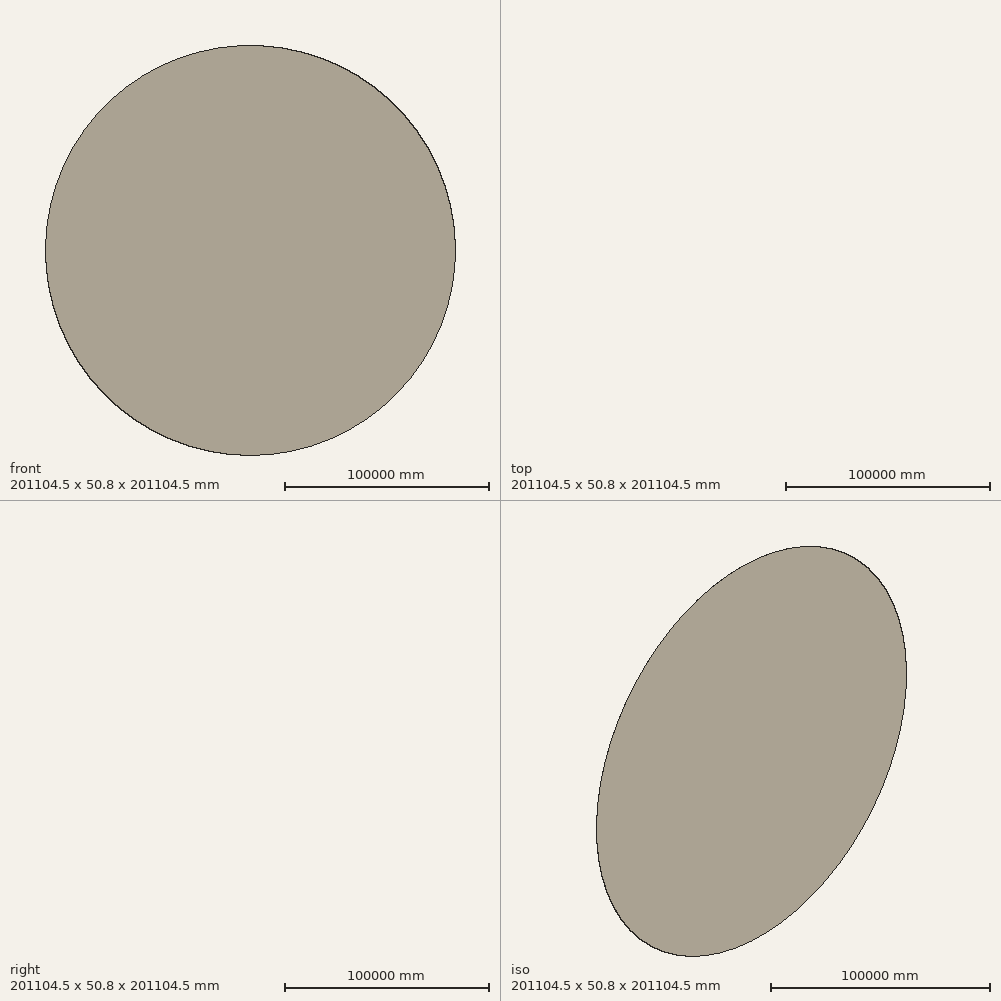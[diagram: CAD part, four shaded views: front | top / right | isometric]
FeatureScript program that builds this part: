
annotation { "Feature Type Name" : "Feature", "Feature Type Description" : "" }
export const myFeature = defineFeature(function(context is Context, id is Id, definition is map)
    precondition{}
    {
        {
            var Q0;
            Q0=qCreatedBy(makeId("Front.planeOp"),FACE);
            var sketch = newSketch(context, id + "F0", { "sketchPlane" : qUnion([Q0])});
            skCircle(sketch, "E0", {"center": v(0, 0) * mm, "radius": 100552.25 * mm});
            skSolve(sketch);
        }
        {
            var Q0;
            Q0=makeQuery(id+"F0.imprint","IMPRINT",FACE,{"disambiguationData":[TD([[makeQuery(id+"F0.imprint","IMPRINT",EDGE,{"derivedFrom":sQuery(id+"F0.wireOp",EDGE,"E0")}),1.0]])]});
            var sketch = newSketch(context, id + "F1", { "sketchPlane" : qUnion([Q0])});
            skCircle(sketch, "E1.0", {"center": v(0, 0) * mm, "radius": 100552.25 * mm});
            skLineSegment(sketch, "E2", {"start": v(0, 100552.25) * mm, "end": v(25.4, 100552.25) * mm});
            skLineSegment(sketch, "E3", {"start": v(25.4, 100552.25) * mm, "end": v(50.8, 100552.25) * mm});
            skSolve(sketch);
        }
        {
            var Q0;
            Q0=makeQuery(id+"F0.imprint","IMPRINT",FACE,{"disambiguationData":[TD([[makeQuery(id+"F0.imprint","IMPRINT",EDGE,{"derivedFrom":sQuery(id+"F0.wireOp",EDGE,"E0")}),1.0]])]});
            extrude(context, id + "F2", {"entities" : qUnion([Q0]), "depth" : 25.4 * mm, "offsetDistance" : 25.4 * mm});
        }
        {
            var Q0;
            Q0=makeQuery(id+"F2.opExtrude","CAP_FACE",FACE,{"disambiguationData":[OSD([sQuery(id+"F0.wireOp",EDGE,"E0")])],"isStart":false});
            var sketch = newSketch(context, id + "F3", { "sketchPlane" : qUnion([Q0])});
            skPoint(sketch, "E4.0", {"position": v(25.4, 100552.25) * mm});
            skPoint(sketch, "E5.0", {"position": v(50.8, 100552.25) * mm});
            skLineSegment(sketch, "E6", {"start": v(25.4, 100552.25) * mm, "end": v(25.4, 100550.27) * mm});
            skLineSegment(sketch, "E7", {"start": v(25.4, 100550.27) * mm, "end": v(24.14, 100550.27) * mm});
            skLineSegment(sketch, "E8", {"start": v(24.14, 100550.27) * mm, "end": v(24.14, 100552.25) * mm});
            skLineSegment(sketch, "E9", {"start": v(24.14, 100552.25) * mm, "end": v(25.4, 100552.25) * mm});
            skLineSegment(sketch, "E10", {"start": v(50.8, 100552.25) * mm, "end": v(50.8, 100549.15) * mm});
            skLineSegment(sketch, "E11", {"start": v(50.8, 100549.15) * mm, "end": v(49.75, 100549.15) * mm});
            skLineSegment(sketch, "E12", {"start": v(49.75, 100549.15) * mm, "end": v(49.75, 100552.25) * mm});
            skLineSegment(sketch, "E13", {"start": v(49.75, 100552.25) * mm, "end": v(50.8, 100552.25) * mm});
            skSolve(sketch);
        }
        {
            var Q0;
            {var subQ0=sQuery(id+"F3.wireOp",EDGE,"E7");Q0=makeQuery(id+"F3.imprint","IMPRINT",FACE,{"disambiguationData":[TD([[makeQuery(id+"F3.imprint","IMPRINT",EDGE,{"derivedFrom":subQ0}),-1.0]])]});}
            var Q1;
            {var subQ0=sQuery(id+"F3.wireOp",EDGE,"E11");Q1=makeQuery(id+"F3.imprint","IMPRINT",FACE,{"disambiguationData":[TD([[makeQuery(id+"F3.imprint","IMPRINT",EDGE,{"derivedFrom":subQ0}),-1.0]])]});}
            extrude(context, id + "F4", {"entities" : qUnion([Q0, Q1]), "depth" : 25.4 * mm, "offsetDistance" : 25.4 * mm});
        }
    });
